# Revit family: Faucet_Single_Control-American_Standard-Pekoe-4332.300
name_source: partatom
category: Plumbing Fixtures
units: mm (PartAtom-declared; Revit-internal decimal feet)

## family parameters
Always vertical = No
Cut with Voids When Loaded = No
OmniClass Number = 23.45.55.14
OmniClass Title = Single Faucets
Part Type = Normal
Room Calculation Point = No
Round Connector Dimension = Use Diameter
Shared = Yes
Work Plane-Based = Yes

## types (1)
- 4332.300
    ADA Compliant = Yes
    Assembly Code = D2020300
    CW Connection = Yes
    CWFU = 1.5
    Cold Water Connection Diameter = 1/2"
    Default Elevation = 0"
    Description = Pekoe Single Control Kitchen Faucet With Pull-Down Spray.
    HW Connection = Yes
    HWFU = 1.5
    Height = 15 1/2"
    Hot Water Connection Diameter = 1/2"
    Length = 8"
    Manufacturer = American Standard
    Material = Metal-American Standard-002-Polished Chrome
    Model = 4332.300
    Product Documentation Link = https://www.americanstandard-us.com
    Product Page URL = https://www.americanstandard-us.com
    Revised Date = 02/08/2017
    URL = http://www.americanstandard-us.com
    Vent Connection = No
    WFU = 0
    Waste Connection = No
    Width = 2"

## geometry (parser evidence)
native form markers: Sweep x2
no freeform markers — native parametric forms only
